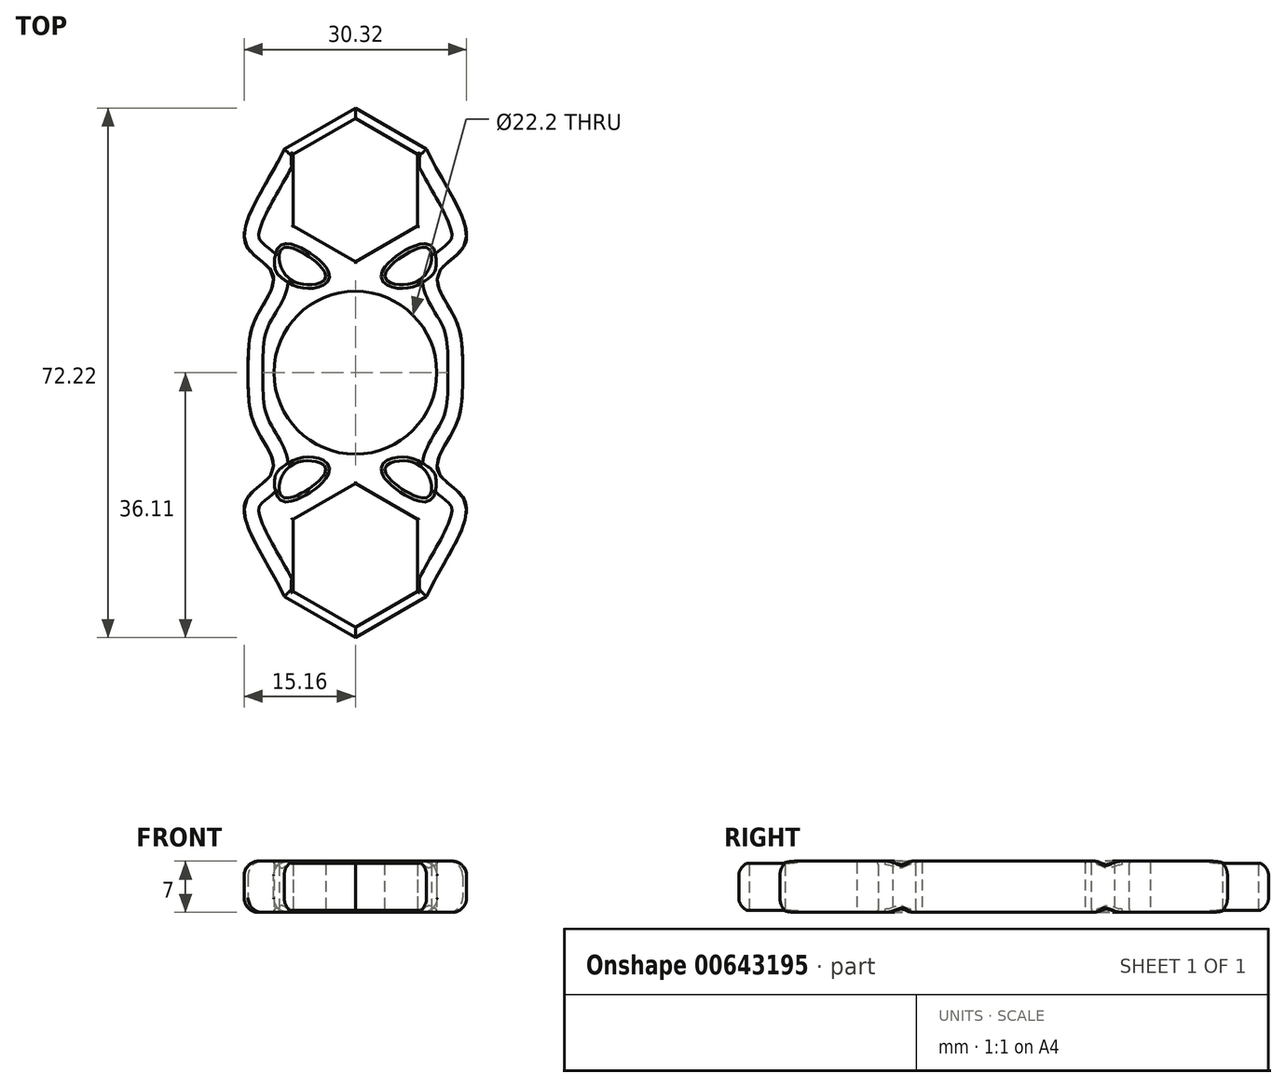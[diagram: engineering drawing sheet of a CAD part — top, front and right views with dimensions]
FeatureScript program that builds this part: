
annotation { "Feature Type Name" : "Feature", "Feature Type Description" : "" }
export const myFeature = defineFeature(function(context is Context, id is Id, definition is map)
    precondition{}
    {
        {
            var Q0;
            Q0=qCreatedBy(makeId("Top.planeOp"),FACE);
            var sketch = newSketch(context, id + "F0", { "sketchPlane" : qUnion([Q0])});
            skCircle(sketch, "E0", {"center": v(0, 0) * mm, "radius": 11.1 * mm});
            skCircle(sketch, "E1.cCircle", {"center": v(0, 24.9) * mm, "radius": 8.5 * mm, "construction": true});
            skLineSegment(sketch, "E1.0", {"start": v(8.5, 29.81) * mm, "end": v(8.5, 20) * mm});
            skLineSegment(sketch, "E1.1", {"start": v(8.5, 20) * mm, "end": v(0, 15.1) * mm});
            skLineSegment(sketch, "E1.2", {"start": v(0, 15.1) * mm, "end": v(-8.5, 20) * mm});
            skLineSegment(sketch, "E1.3", {"start": v(-8.5, 20) * mm, "end": v(-8.5, 29.81) * mm});
            skLineSegment(sketch, "E1.4", {"start": v(-8.5, 29.81) * mm, "end": v(0, 34.72) * mm});
            skLineSegment(sketch, "E1.5", {"start": v(0, 34.72) * mm, "end": v(8.5, 29.81) * mm});
            skPoint(sketch, "E1.0.midPoint", {"position": v(8.5, 24.9) * mm});
            skCircle(sketch, "E2.cCircle", {"center": v(0, 24.9) * mm, "radius": 9.7 * mm, "construction": true});
            skLineSegment(sketch, "E2.0", {"start": v(9.7, 30.51) * mm, "end": v(9.7, 19.3) * mm});
            skLineSegment(sketch, "E2.1", {"start": v(9.7, 19.3) * mm, "end": v(0, 13.7) * mm});
            skLineSegment(sketch, "E2.2", {"start": v(0, 13.7) * mm, "end": v(-9.7, 19.3) * mm});
            skLineSegment(sketch, "E2.3", {"start": v(-9.7, 19.3) * mm, "end": v(-9.7, 30.51) * mm});
            skLineSegment(sketch, "E2.4", {"start": v(-9.7, 30.51) * mm, "end": v(0, 36.11) * mm});
            skLineSegment(sketch, "E2.5", {"start": v(0, 36.11) * mm, "end": v(9.7, 30.51) * mm});
            skPoint(sketch, "E2.0.midPoint", {"position": v(9.7, 24.9) * mm});
            skCircle(sketch, "E3", {"center": v(0, 0) * mm, "radius": 12.3 * mm});
            skFitSpline(sketch, "E4", {"points": [v(-14.63, 0) * mm, v(-13.28, 8.02) * mm, v(-11.25, 13.43) * mm, v(-15.03, 17.75) * mm, v(-9.7, 30.51) * mm], "startDerivative": vector(0, 53.93) * mm, "endDerivative": vector(19.66, 42.9) * mm});
            skLineSegment(sketch, "E5.MirrorCS", {"start": v(9.7, 19.3) * mm, "end": v(9.7, 30.51) * mm});
            skFitSpline(sketch, "E6.MirrorCS", {"points": [v(14.63, 0) * mm, v(13.28, 8.02) * mm, v(11.25, 13.43) * mm, v(15.03, 17.75) * mm, v(9.7, 30.51) * mm], "startDerivative": vector(0, 53.93) * mm, "endDerivative": vector(-19.66, 42.9) * mm});
            skLineSegment(sketch, "E7.MirrorCS", {"start": v(9.7, -19.3) * mm, "end": v(9.7, -30.51) * mm});
            skLineSegment(sketch, "E8.MirrorCS", {"start": v(8.5, -20) * mm, "end": v(0, -15.1) * mm});
            skLineSegment(sketch, "E9.MirrorCS", {"start": v(-8.5, -20) * mm, "end": v(-8.5, -29.81) * mm});
            skLineSegment(sketch, "E10.MirrorCS", {"start": v(9.7, -30.51) * mm, "end": v(9.7, -19.3) * mm});
            skLineSegment(sketch, "E11.MirrorCS", {"start": v(-9.7, -30.51) * mm, "end": v(0, -36.11) * mm});
            skLineSegment(sketch, "E12.MirrorCS", {"start": v(0, -15.1) * mm, "end": v(-8.5, -20) * mm});
            skCircle(sketch, "E13.MirrorC", {"center": v(0, -24.9) * mm, "radius": 9.7 * mm, "construction": true});
            skLineSegment(sketch, "E14.MirrorCS", {"start": v(0, -36.11) * mm, "end": v(9.7, -30.51) * mm});
            skPoint(sketch, "E15.MirrorP", {"position": v(9.7, -24.9) * mm});
            skLineSegment(sketch, "E16.MirrorCS", {"start": v(-9.7, -19.3) * mm, "end": v(-9.7, -30.51) * mm});
            skPoint(sketch, "E17.MirrorP", {"position": v(8.5, -24.9) * mm});
            skCircle(sketch, "E18.MirrorC", {"center": v(0, -24.9) * mm, "radius": 8.5 * mm, "construction": true});
            skLineSegment(sketch, "E19.MirrorCS", {"start": v(0, -34.72) * mm, "end": v(8.5, -29.81) * mm});
            skLineSegment(sketch, "E20.MirrorCS", {"start": v(8.5, -29.81) * mm, "end": v(8.5, -20) * mm});
            skLineSegment(sketch, "E21.MirrorCS", {"start": v(-8.5, -29.81) * mm, "end": v(0, -34.72) * mm});
            skLineSegment(sketch, "E22.MirrorCS", {"start": v(9.7, -19.3) * mm, "end": v(0, -13.7) * mm});
            skLineSegment(sketch, "E23.MirrorCS", {"start": v(0, -13.7) * mm, "end": v(-9.7, -19.3) * mm});
            skFitSpline(sketch, "E24.MirrorCS", {"points": [v(14.63, 0) * mm, v(13.28, -8.02) * mm, v(11.25, -13.43) * mm, v(15.03, -17.75) * mm, v(9.7, -30.51) * mm], "startDerivative": vector(0, -53.93) * mm, "endDerivative": vector(-19.66, -42.9) * mm});
            skFitSpline(sketch, "E25.MirrorCS", {"points": [v(-14.63, 0) * mm, v(-13.28, -8.02) * mm, v(-11.25, -13.43) * mm, v(-15.03, -17.75) * mm, v(-9.7, -30.51) * mm], "startDerivative": vector(0, -53.93) * mm, "endDerivative": vector(19.66, -42.9) * mm});
            skFitSpline(sketch, "E26", {"points": [v(-7.78, 12.2) * mm, v(-4, 13.17) * mm, v(-9.47, 17.1) * mm, v(-10.36, 15.26) * mm, v(-7.78, 12.2) * mm]});
            skFitSpline(sketch, "E27.MirrorC", {"points": [v(7.78, 12.2) * mm, v(4, 13.17) * mm, v(9.47, 17.1) * mm, v(10.36, 15.26) * mm, v(7.78, 12.2) * mm]});
            skFitSpline(sketch, "E28.MirrorC", {"points": [v(-7.78, -12.2) * mm, v(-4, -13.17) * mm, v(-9.47, -17.1) * mm, v(-10.36, -15.26) * mm, v(-7.78, -12.2) * mm]});
            skFitSpline(sketch, "E29.MirrorC", {"points": [v(7.78, -12.2) * mm, v(4, -13.17) * mm, v(9.47, -17.1) * mm, v(10.36, -15.26) * mm, v(7.78, -12.2) * mm]});
            skSolve(sketch);
        }
        {
            var Q0;
            Q0=makeQuery(id+"F0.imprint","IMPRINT",FACE,{"disambiguationData":[TD([[makeQuery(id+"F0.imprint","IMPRINT",EDGE,{"derivedFrom":sQuery(id+"F0.wireOp",EDGE,"E2.1")}),1.0]])]});
            var Q1;
            Q1=makeQuery(id+"F0.imprint","IMPRINT",FACE,{"disambiguationData":[TD([[makeQuery(id+"F0.imprint","IMPRINT",EDGE,{"derivedFrom":sQuery(id+"F0.wireOp",EDGE,"E1.0")}),1.0]])]});
            var Q2;
            Q2=makeQuery(id+"F0.imprint","IMPRINT",FACE,{"disambiguationData":[TD([[makeQuery(id+"F0.imprint","IMPRINT",EDGE,{"derivedFrom":sQuery(id+"F0.wireOp",EDGE,"E0")}),-1.0]])]});
            var Q3;
            Q3=makeQuery(id+"F0.imprint","IMPRINT",FACE,{"disambiguationData":[TD([[makeQuery(id+"F0.imprint","IMPRINT",EDGE,{"derivedFrom":sQuery(id+"F0.wireOp",EDGE,"E8.MirrorCS")}),-1.0]])]});
            extrude(context, id + "F1", {"entities" : qUnion([Q0, Q1, Q2, Q3]), "depth" : 7 * mm, "offsetDistance" : 25 * mm});
        }
        {
            var Q0;
            Q0=makeQuery(id+"F1.opExtrude","CAP_EDGE",EDGE,{"disambiguationData":[OSD([sQuery(id+"F0.wireOp",EDGE,"E4")])],"isStart":false});
            var Q1;
            Q1=makeQuery(id+"F1.opExtrude","CAP_EDGE",EDGE,{"disambiguationData":[OSD([sQuery(id+"F0.wireOp",EDGE,"E25.MirrorCS")])],"isStart":false});
            var Q2;
            Q2=makeQuery(id+"F1.opExtrude","CAP_EDGE",EDGE,{"disambiguationData":[OSD([sQuery(id+"F0.wireOp",EDGE,"E11.MirrorCS")])],"isStart":false});
            var Q3;
            Q3=makeQuery(id+"F1.opExtrude","CAP_EDGE",EDGE,{"disambiguationData":[OSD([sQuery(id+"F0.wireOp",EDGE,"E14.MirrorCS")])],"isStart":false});
            var Q4;
            Q4=makeQuery(id+"F1.opExtrude","CAP_EDGE",EDGE,{"disambiguationData":[OSD([sQuery(id+"F0.wireOp",EDGE,"E24.MirrorCS")])],"isStart":false});
            var Q5;
            Q5=makeQuery(id+"F1.opExtrude","CAP_EDGE",EDGE,{"disambiguationData":[OSD([sQuery(id+"F0.wireOp",EDGE,"E2.5")])],"isStart":false});
            var Q6;
            Q6=makeQuery(id+"F1.opExtrude","CAP_EDGE",EDGE,{"disambiguationData":[OSD([sQuery(id+"F0.wireOp",EDGE,"E2.4")])],"isStart":false});
            var Q7;
            Q7=makeQuery(id+"F1.opExtrude","CAP_EDGE",EDGE,{"disambiguationData":[OSD([sQuery(id+"F0.wireOp",EDGE,"E25.MirrorCS")])],"isStart":true});
            var Q8;
            Q8=makeQuery(id+"F1.opExtrude","CAP_EDGE",EDGE,{"disambiguationData":[OSD([sQuery(id+"F0.wireOp",EDGE,"E4")])],"isStart":true});
            var Q9;
            Q9=makeQuery(id+"F1.opExtrude","CAP_EDGE",EDGE,{"disambiguationData":[OSD([sQuery(id+"F0.wireOp",EDGE,"E6.MirrorCS")])],"isStart":true});
            var Q10;
            Q10=makeQuery(id+"F1.opExtrude","CAP_EDGE",EDGE,{"disambiguationData":[OSD([sQuery(id+"F0.wireOp",EDGE,"E2.5")])],"isStart":true});
            var Q11;
            Q11=makeQuery(id+"F1.opExtrude","CAP_EDGE",EDGE,{"disambiguationData":[OSD([sQuery(id+"F0.wireOp",EDGE,"E2.4")])],"isStart":true});
            var Q12;
            Q12=makeQuery(id+"F1.opExtrude","CAP_EDGE",EDGE,{"disambiguationData":[OSD([sQuery(id+"F0.wireOp",EDGE,"E14.MirrorCS")])],"isStart":true});
            var Q13;
            Q13=makeQuery(id+"F1.opExtrude","CAP_EDGE",EDGE,{"disambiguationData":[OSD([sQuery(id+"F0.wireOp",EDGE,"E11.MirrorCS")])],"isStart":true});
            var Q14;
            Q14=makeQuery(id+"F1.opExtrude","CAP_EDGE",EDGE,{"disambiguationData":[OSD([sQuery(id+"F0.wireOp",EDGE,"E24.MirrorCS")])],"isStart":true});
            fillet(context, id + "F2", {"entities" : qUnion([Q0, Q1, Q2, Q3, Q4, Q5, Q6, Q7, Q8, Q9, Q10, Q11, Q12, Q13, Q14]), "radius" : 2 * mm, "tangentPropagation" : true, "allowEdgeOverflow" : false});
        }
        {
            var Q0;
            Q0=makeQuery(id+"F1.opExtrude","SWEPT_FACE",FACE,{"disambiguationData":[OSD([sQuery(id+"F0.wireOp",EDGE,"E29.MirrorC")])]});
            var Q1;
            Q1=makeQuery(id+"F1.opExtrude","SWEPT_FACE",FACE,{"disambiguationData":[OSD([sQuery(id+"F0.wireOp",EDGE,"E28.MirrorC")])]});
            var Q2;
            Q2=makeQuery(id+"F1.opExtrude","SWEPT_FACE",FACE,{"disambiguationData":[OSD([sQuery(id+"F0.wireOp",EDGE,"E27.MirrorC")])]});
            var Q3;
            Q3=makeQuery(id+"F1.opExtrude","SWEPT_FACE",FACE,{"disambiguationData":[OSD([sQuery(id+"F0.wireOp",EDGE,"E26")])]});
            fillet(context, id + "F3", {"entities" : qUnion([Q0, Q1, Q2, Q3]), "radius" : 0.5 * mm, "tangentPropagation" : true, "allowEdgeOverflow" : false});
        }
        {
            var Q0;
            Q0=makeQuery(id+"F1.opExtrude","CAP_EDGE",EDGE,{"disambiguationData":[OSD([sQuery(id+"F0.wireOp",EDGE,"E12.MirrorCS")])],"isStart":true});
            var Q1;
            Q1=makeQuery(id+"F1.opExtrude","CAP_EDGE",EDGE,{"disambiguationData":[OSD([sQuery(id+"F0.wireOp",EDGE,"E8.MirrorCS")])],"isStart":true});
            var Q2;
            Q2=makeQuery(id+"F1.opExtrude","CAP_EDGE",EDGE,{"disambiguationData":[OSD([sQuery(id+"F0.wireOp",EDGE,"E9.MirrorCS")])],"isStart":true});
            var Q3;
            Q3=makeQuery(id+"F2.opFillet","BLEND_EDGE",EDGE,{"blendedFrom":[makeQuery(id+"F1.opExtrude","CAP_EDGE",EDGE,{"disambiguationData":[OSD([sQuery(id+"F0.wireOp",EDGE,"E11.MirrorCS")])],"isStart":true}),makeQuery(id+"F1.opExtrude","SWEPT_FACE",FACE,{"disambiguationData":[OSD([sQuery(id+"F0.wireOp",EDGE,"E21.MirrorCS")])]})],"blendedInto":[makeQuery(id+"F1.opExtrude","SWEPT_FACE",FACE,{"disambiguationData":[OSD([sQuery(id+"F0.wireOp",EDGE,"E21.MirrorCS")])]})]});
            var Q4;
            Q4=makeQuery(id+"F2.opFillet","BLEND_EDGE",EDGE,{"blendedFrom":[makeQuery(id+"F1.opExtrude","CAP_EDGE",EDGE,{"disambiguationData":[OSD([sQuery(id+"F0.wireOp",EDGE,"E14.MirrorCS")])],"isStart":true}),makeQuery(id+"F1.opExtrude","SWEPT_FACE",FACE,{"disambiguationData":[OSD([sQuery(id+"F0.wireOp",EDGE,"E19.MirrorCS")])]})],"blendedInto":[makeQuery(id+"F1.opExtrude","SWEPT_FACE",FACE,{"disambiguationData":[OSD([sQuery(id+"F0.wireOp",EDGE,"E19.MirrorCS")])]})]});
            var Q5;
            Q5=makeQuery(id+"F1.opExtrude","CAP_EDGE",EDGE,{"disambiguationData":[OSD([sQuery(id+"F0.wireOp",EDGE,"E8.MirrorCS")])],"isStart":false});
            var Q6;
            Q6=makeQuery(id+"F1.opExtrude","CAP_EDGE",EDGE,{"disambiguationData":[OSD([sQuery(id+"F0.wireOp",EDGE,"E20.MirrorCS")])],"isStart":false});
            var Q7;
            Q7=makeQuery(id+"F2.opFillet","BLEND_EDGE",EDGE,{"blendedFrom":[makeQuery(id+"F1.opExtrude","CAP_EDGE",EDGE,{"disambiguationData":[OSD([sQuery(id+"F0.wireOp",EDGE,"E14.MirrorCS")])],"isStart":false}),makeQuery(id+"F1.opExtrude","SWEPT_FACE",FACE,{"disambiguationData":[OSD([sQuery(id+"F0.wireOp",EDGE,"E19.MirrorCS")])]})],"blendedInto":[makeQuery(id+"F1.opExtrude","SWEPT_FACE",FACE,{"disambiguationData":[OSD([sQuery(id+"F0.wireOp",EDGE,"E19.MirrorCS")])]})]});
            var Q8;
            Q8=makeQuery(id+"F2.opFillet","BLEND_EDGE",EDGE,{"blendedFrom":[makeQuery(id+"F1.opExtrude","CAP_EDGE",EDGE,{"disambiguationData":[OSD([sQuery(id+"F0.wireOp",EDGE,"E24.MirrorCS")])],"isStart":false}),makeQuery(id+"F1.opExtrude","SWEPT_FACE",FACE,{"disambiguationData":[OSD([sQuery(id+"F0.wireOp",EDGE,"E20.MirrorCS")])]})],"blendedInto":[makeQuery(id+"F1.opExtrude","SWEPT_FACE",FACE,{"disambiguationData":[OSD([sQuery(id+"F0.wireOp",EDGE,"E20.MirrorCS")])]})]});
            var Q9;
            Q9=makeQuery(id+"F2.opFillet","BLEND_EDGE",EDGE,{"blendedFrom":[makeQuery(id+"F1.opExtrude","CAP_EDGE",EDGE,{"disambiguationData":[OSD([sQuery(id+"F0.wireOp",EDGE,"E14.MirrorCS")])],"isStart":false}),makeQuery(id+"F1.opExtrude","SWEPT_FACE",FACE,{"disambiguationData":[OSD([sQuery(id+"F0.wireOp",EDGE,"E20.MirrorCS")])]})],"blendedInto":[makeQuery(id+"F1.opExtrude","SWEPT_FACE",FACE,{"disambiguationData":[OSD([sQuery(id+"F0.wireOp",EDGE,"E20.MirrorCS")])]})]});
            var Q10;
            Q10=makeQuery(id+"F2.opFillet","BLEND_EDGE",EDGE,{"blendedFrom":[makeQuery(id+"F1.opExtrude","CAP_EDGE",EDGE,{"disambiguationData":[OSD([sQuery(id+"F0.wireOp",EDGE,"E11.MirrorCS")])],"isStart":false}),makeQuery(id+"F1.opExtrude","SWEPT_FACE",FACE,{"disambiguationData":[OSD([sQuery(id+"F0.wireOp",EDGE,"E21.MirrorCS")])]})],"blendedInto":[makeQuery(id+"F1.opExtrude","SWEPT_FACE",FACE,{"disambiguationData":[OSD([sQuery(id+"F0.wireOp",EDGE,"E21.MirrorCS")])]})]});
            var Q11;
            Q11=makeQuery(id+"F1.opExtrude","CAP_EDGE",EDGE,{"disambiguationData":[OSD([sQuery(id+"F0.wireOp",EDGE,"E9.MirrorCS")])],"isStart":false});
            var Q12;
            Q12=makeQuery(id+"F2.opFillet","BLEND_EDGE",EDGE,{"blendedFrom":[makeQuery(id+"F1.opExtrude","CAP_EDGE",EDGE,{"disambiguationData":[OSD([sQuery(id+"F0.wireOp",EDGE,"E25.MirrorCS")])],"isStart":false}),makeQuery(id+"F1.opExtrude","SWEPT_FACE",FACE,{"disambiguationData":[OSD([sQuery(id+"F0.wireOp",EDGE,"E9.MirrorCS")])]})],"blendedInto":[makeQuery(id+"F1.opExtrude","SWEPT_FACE",FACE,{"disambiguationData":[OSD([sQuery(id+"F0.wireOp",EDGE,"E9.MirrorCS")])]})]});
            var Q13;
            Q13=makeQuery(id+"F2.opFillet","BLEND_EDGE",EDGE,{"blendedFrom":[makeQuery(id+"F1.opExtrude","CAP_EDGE",EDGE,{"disambiguationData":[OSD([sQuery(id+"F0.wireOp",EDGE,"E11.MirrorCS")])],"isStart":false}),makeQuery(id+"F1.opExtrude","SWEPT_FACE",FACE,{"disambiguationData":[OSD([sQuery(id+"F0.wireOp",EDGE,"E9.MirrorCS")])]})],"blendedInto":[makeQuery(id+"F1.opExtrude","SWEPT_FACE",FACE,{"disambiguationData":[OSD([sQuery(id+"F0.wireOp",EDGE,"E9.MirrorCS")])]})]});
            var Q14;
            Q14=makeQuery(id+"F1.opExtrude","CAP_EDGE",EDGE,{"disambiguationData":[OSD([sQuery(id+"F0.wireOp",EDGE,"E12.MirrorCS")])],"isStart":false});
            var Q15;
            Q15=makeQuery(id+"F1.opExtrude","CAP_EDGE",EDGE,{"disambiguationData":[OSD([sQuery(id+"F0.wireOp",EDGE,"E20.MirrorCS")])],"isStart":true});
            var Q16;
            Q16=makeQuery(id+"F2.opFillet","BLEND_EDGE",EDGE,{"blendedFrom":[makeQuery(id+"F1.opExtrude","CAP_EDGE",EDGE,{"disambiguationData":[OSD([sQuery(id+"F0.wireOp",EDGE,"E24.MirrorCS")])],"isStart":true}),makeQuery(id+"F1.opExtrude","SWEPT_FACE",FACE,{"disambiguationData":[OSD([sQuery(id+"F0.wireOp",EDGE,"E20.MirrorCS")])]})],"blendedInto":[makeQuery(id+"F1.opExtrude","SWEPT_FACE",FACE,{"disambiguationData":[OSD([sQuery(id+"F0.wireOp",EDGE,"E20.MirrorCS")])]})]});
            var Q17;
            Q17=makeQuery(id+"F2.opFillet","BLEND_EDGE",EDGE,{"blendedFrom":[makeQuery(id+"F1.opExtrude","CAP_EDGE",EDGE,{"disambiguationData":[OSD([sQuery(id+"F0.wireOp",EDGE,"E14.MirrorCS")])],"isStart":true}),makeQuery(id+"F1.opExtrude","SWEPT_FACE",FACE,{"disambiguationData":[OSD([sQuery(id+"F0.wireOp",EDGE,"E20.MirrorCS")])]})],"blendedInto":[makeQuery(id+"F1.opExtrude","SWEPT_FACE",FACE,{"disambiguationData":[OSD([sQuery(id+"F0.wireOp",EDGE,"E20.MirrorCS")])]})]});
            var Q18;
            Q18=makeQuery(id+"F2.opFillet","BLEND_EDGE",EDGE,{"blendedFrom":[makeQuery(id+"F1.opExtrude","CAP_EDGE",EDGE,{"disambiguationData":[OSD([sQuery(id+"F0.wireOp",EDGE,"E25.MirrorCS")])],"isStart":true}),makeQuery(id+"F1.opExtrude","SWEPT_FACE",FACE,{"disambiguationData":[OSD([sQuery(id+"F0.wireOp",EDGE,"E9.MirrorCS")])]})],"blendedInto":[makeQuery(id+"F1.opExtrude","SWEPT_FACE",FACE,{"disambiguationData":[OSD([sQuery(id+"F0.wireOp",EDGE,"E9.MirrorCS")])]})]});
            var Q19;
            Q19=makeQuery(id+"F2.opFillet","BLEND_EDGE",EDGE,{"blendedFrom":[makeQuery(id+"F1.opExtrude","CAP_EDGE",EDGE,{"disambiguationData":[OSD([sQuery(id+"F0.wireOp",EDGE,"E11.MirrorCS")])],"isStart":true}),makeQuery(id+"F1.opExtrude","SWEPT_FACE",FACE,{"disambiguationData":[OSD([sQuery(id+"F0.wireOp",EDGE,"E9.MirrorCS")])]})],"blendedInto":[makeQuery(id+"F1.opExtrude","SWEPT_FACE",FACE,{"disambiguationData":[OSD([sQuery(id+"F0.wireOp",EDGE,"E9.MirrorCS")])]})]});
            var Q20;
            Q20=makeQuery(id+"F2.opFillet","BLEND_EDGE",EDGE,{"blendedFrom":[makeQuery(id+"F1.opExtrude","CAP_EDGE",EDGE,{"disambiguationData":[OSD([sQuery(id+"F0.wireOp",EDGE,"E2.4")])],"isStart":true}),makeQuery(id+"F1.opExtrude","SWEPT_FACE",FACE,{"disambiguationData":[OSD([sQuery(id+"F0.wireOp",EDGE,"E1.4")])]})],"blendedInto":[makeQuery(id+"F1.opExtrude","SWEPT_FACE",FACE,{"disambiguationData":[OSD([sQuery(id+"F0.wireOp",EDGE,"E1.4")])]})]});
            var Q21;
            Q21=makeQuery(id+"F2.opFillet","BLEND_EDGE",EDGE,{"blendedFrom":[makeQuery(id+"F1.opExtrude","CAP_EDGE",EDGE,{"disambiguationData":[OSD([sQuery(id+"F0.wireOp",EDGE,"E2.4")])],"isStart":true}),makeQuery(id+"F1.opExtrude","SWEPT_FACE",FACE,{"disambiguationData":[OSD([sQuery(id+"F0.wireOp",EDGE,"E1.3")])]})],"blendedInto":[makeQuery(id+"F1.opExtrude","SWEPT_FACE",FACE,{"disambiguationData":[OSD([sQuery(id+"F0.wireOp",EDGE,"E1.3")])]})]});
            var Q22;
            Q22=makeQuery(id+"F2.opFillet","BLEND_EDGE",EDGE,{"blendedFrom":[makeQuery(id+"F1.opExtrude","CAP_EDGE",EDGE,{"disambiguationData":[OSD([sQuery(id+"F0.wireOp",EDGE,"E4")])],"isStart":true}),makeQuery(id+"F1.opExtrude","SWEPT_FACE",FACE,{"disambiguationData":[OSD([sQuery(id+"F0.wireOp",EDGE,"E1.3")])]})],"blendedInto":[makeQuery(id+"F1.opExtrude","SWEPT_FACE",FACE,{"disambiguationData":[OSD([sQuery(id+"F0.wireOp",EDGE,"E1.3")])]})]});
            var Q23;
            Q23=makeQuery(id+"F1.opExtrude","CAP_EDGE",EDGE,{"disambiguationData":[OSD([sQuery(id+"F0.wireOp",EDGE,"E1.3")])],"isStart":true});
            var Q24;
            Q24=makeQuery(id+"F1.opExtrude","CAP_EDGE",EDGE,{"disambiguationData":[OSD([sQuery(id+"F0.wireOp",EDGE,"E1.2")])],"isStart":true});
            var Q25;
            Q25=makeQuery(id+"F1.opExtrude","CAP_EDGE",EDGE,{"disambiguationData":[OSD([sQuery(id+"F0.wireOp",EDGE,"E1.1")])],"isStart":true});
            var Q26;
            Q26=makeQuery(id+"F1.opExtrude","CAP_EDGE",EDGE,{"disambiguationData":[OSD([sQuery(id+"F0.wireOp",EDGE,"E1.0")])],"isStart":true});
            var Q27;
            Q27=makeQuery(id+"F2.opFillet","BLEND_EDGE",EDGE,{"blendedFrom":[makeQuery(id+"F1.opExtrude","CAP_EDGE",EDGE,{"disambiguationData":[OSD([sQuery(id+"F0.wireOp",EDGE,"E6.MirrorCS")])],"isStart":true}),makeQuery(id+"F1.opExtrude","SWEPT_FACE",FACE,{"disambiguationData":[OSD([sQuery(id+"F0.wireOp",EDGE,"E1.0")])]})],"blendedInto":[makeQuery(id+"F1.opExtrude","SWEPT_FACE",FACE,{"disambiguationData":[OSD([sQuery(id+"F0.wireOp",EDGE,"E1.0")])]})]});
            var Q28;
            Q28=makeQuery(id+"F2.opFillet","BLEND_EDGE",EDGE,{"blendedFrom":[makeQuery(id+"F1.opExtrude","CAP_EDGE",EDGE,{"disambiguationData":[OSD([sQuery(id+"F0.wireOp",EDGE,"E2.5")])],"isStart":true}),makeQuery(id+"F1.opExtrude","SWEPT_FACE",FACE,{"disambiguationData":[OSD([sQuery(id+"F0.wireOp",EDGE,"E1.0")])]})],"blendedInto":[makeQuery(id+"F1.opExtrude","SWEPT_FACE",FACE,{"disambiguationData":[OSD([sQuery(id+"F0.wireOp",EDGE,"E1.0")])]})]});
            var Q29;
            Q29=makeQuery(id+"F2.opFillet","BLEND_EDGE",EDGE,{"blendedFrom":[makeQuery(id+"F1.opExtrude","CAP_EDGE",EDGE,{"disambiguationData":[OSD([sQuery(id+"F0.wireOp",EDGE,"E2.5")])],"isStart":true}),makeQuery(id+"F1.opExtrude","SWEPT_FACE",FACE,{"disambiguationData":[OSD([sQuery(id+"F0.wireOp",EDGE,"E1.5")])]})],"blendedInto":[makeQuery(id+"F1.opExtrude","SWEPT_FACE",FACE,{"disambiguationData":[OSD([sQuery(id+"F0.wireOp",EDGE,"E1.5")])]})]});
            var Q30;
            Q30=makeQuery(id+"F1.opExtrude","CAP_EDGE",EDGE,{"disambiguationData":[OSD([sQuery(id+"F0.wireOp",EDGE,"E1.3")])],"isStart":false});
            var Q31;
            Q31=makeQuery(id+"F2.opFillet","BLEND_EDGE",EDGE,{"blendedFrom":[makeQuery(id+"F1.opExtrude","CAP_EDGE",EDGE,{"disambiguationData":[OSD([sQuery(id+"F0.wireOp",EDGE,"E4")])],"isStart":false}),makeQuery(id+"F1.opExtrude","SWEPT_FACE",FACE,{"disambiguationData":[OSD([sQuery(id+"F0.wireOp",EDGE,"E1.3")])]})],"blendedInto":[makeQuery(id+"F1.opExtrude","SWEPT_FACE",FACE,{"disambiguationData":[OSD([sQuery(id+"F0.wireOp",EDGE,"E1.3")])]})]});
            var Q32;
            Q32=makeQuery(id+"F2.opFillet","BLEND_EDGE",EDGE,{"blendedFrom":[makeQuery(id+"F1.opExtrude","CAP_EDGE",EDGE,{"disambiguationData":[OSD([sQuery(id+"F0.wireOp",EDGE,"E2.4")])],"isStart":false}),makeQuery(id+"F1.opExtrude","SWEPT_FACE",FACE,{"disambiguationData":[OSD([sQuery(id+"F0.wireOp",EDGE,"E1.3")])]})],"blendedInto":[makeQuery(id+"F1.opExtrude","SWEPT_FACE",FACE,{"disambiguationData":[OSD([sQuery(id+"F0.wireOp",EDGE,"E1.3")])]})]});
            var Q33;
            Q33=makeQuery(id+"F2.opFillet","BLEND_EDGE",EDGE,{"blendedFrom":[makeQuery(id+"F1.opExtrude","CAP_EDGE",EDGE,{"disambiguationData":[OSD([sQuery(id+"F0.wireOp",EDGE,"E2.4")])],"isStart":false}),makeQuery(id+"F1.opExtrude","SWEPT_FACE",FACE,{"disambiguationData":[OSD([sQuery(id+"F0.wireOp",EDGE,"E1.4")])]})],"blendedInto":[makeQuery(id+"F1.opExtrude","SWEPT_FACE",FACE,{"disambiguationData":[OSD([sQuery(id+"F0.wireOp",EDGE,"E1.4")])]})]});
            var Q34;
            Q34=makeQuery(id+"F2.opFillet","BLEND_EDGE",EDGE,{"blendedFrom":[makeQuery(id+"F1.opExtrude","CAP_EDGE",EDGE,{"disambiguationData":[OSD([sQuery(id+"F0.wireOp",EDGE,"E2.5")])],"isStart":false}),makeQuery(id+"F1.opExtrude","SWEPT_FACE",FACE,{"disambiguationData":[OSD([sQuery(id+"F0.wireOp",EDGE,"E1.5")])]})],"blendedInto":[makeQuery(id+"F1.opExtrude","SWEPT_FACE",FACE,{"disambiguationData":[OSD([sQuery(id+"F0.wireOp",EDGE,"E1.5")])]})]});
            var Q35;
            Q35=makeQuery(id+"F1.opExtrude","CAP_EDGE",EDGE,{"disambiguationData":[OSD([sQuery(id+"F0.wireOp",EDGE,"E1.0")])],"isStart":false});
            var Q36;
            Q36=makeQuery(id+"F1.opExtrude","CAP_EDGE",EDGE,{"disambiguationData":[OSD([sQuery(id+"F0.wireOp",EDGE,"E1.1")])],"isStart":false});
            var Q37;
            Q37=makeQuery(id+"F1.opExtrude","CAP_EDGE",EDGE,{"disambiguationData":[OSD([sQuery(id+"F0.wireOp",EDGE,"E1.2")])],"isStart":false});
            var Q38;
            Q38=makeQuery(id+"F2.opFillet","BLEND_EDGE",EDGE,{"blendedFrom":[makeQuery(id+"F1.opExtrude","CAP_EDGE",EDGE,{"disambiguationData":[OSD([sQuery(id+"F0.wireOp",EDGE,"E2.5")])],"isStart":false}),makeQuery(id+"F1.opExtrude","SWEPT_FACE",FACE,{"disambiguationData":[OSD([sQuery(id+"F0.wireOp",EDGE,"E1.0")])]})],"blendedInto":[makeQuery(id+"F1.opExtrude","SWEPT_FACE",FACE,{"disambiguationData":[OSD([sQuery(id+"F0.wireOp",EDGE,"E1.0")])]})]});
            var Q39;
            Q39=makeQuery(id+"F1.opExtrude","CAP_EDGE",EDGE,{"disambiguationData":[OSD([sQuery(id+"F0.wireOp",EDGE,"E0")])],"isStart":false});
            var Q40;
            Q40=makeQuery(id+"F1.opExtrude","CAP_EDGE",EDGE,{"disambiguationData":[OSD([sQuery(id+"F0.wireOp",EDGE,"E0")])],"isStart":true});
            fillet(context, id + "F4", {"entities" : qUnion([Q0, Q1, Q2, Q3, Q4, Q5, Q6, Q7, Q8, Q9, Q10, Q11, Q12, Q13, Q14, Q15, Q16, Q17, Q18, Q19, Q20, Q21, Q22, Q23, Q24, Q25, Q26, Q27, Q28, Q29, Q30, Q31, Q32, Q33, Q34, Q35, Q36, Q37, Q38, Q39, Q40]), "radius" : 0.2 * mm, "tangentPropagation" : true, "allowEdgeOverflow" : false});
        }
    });
